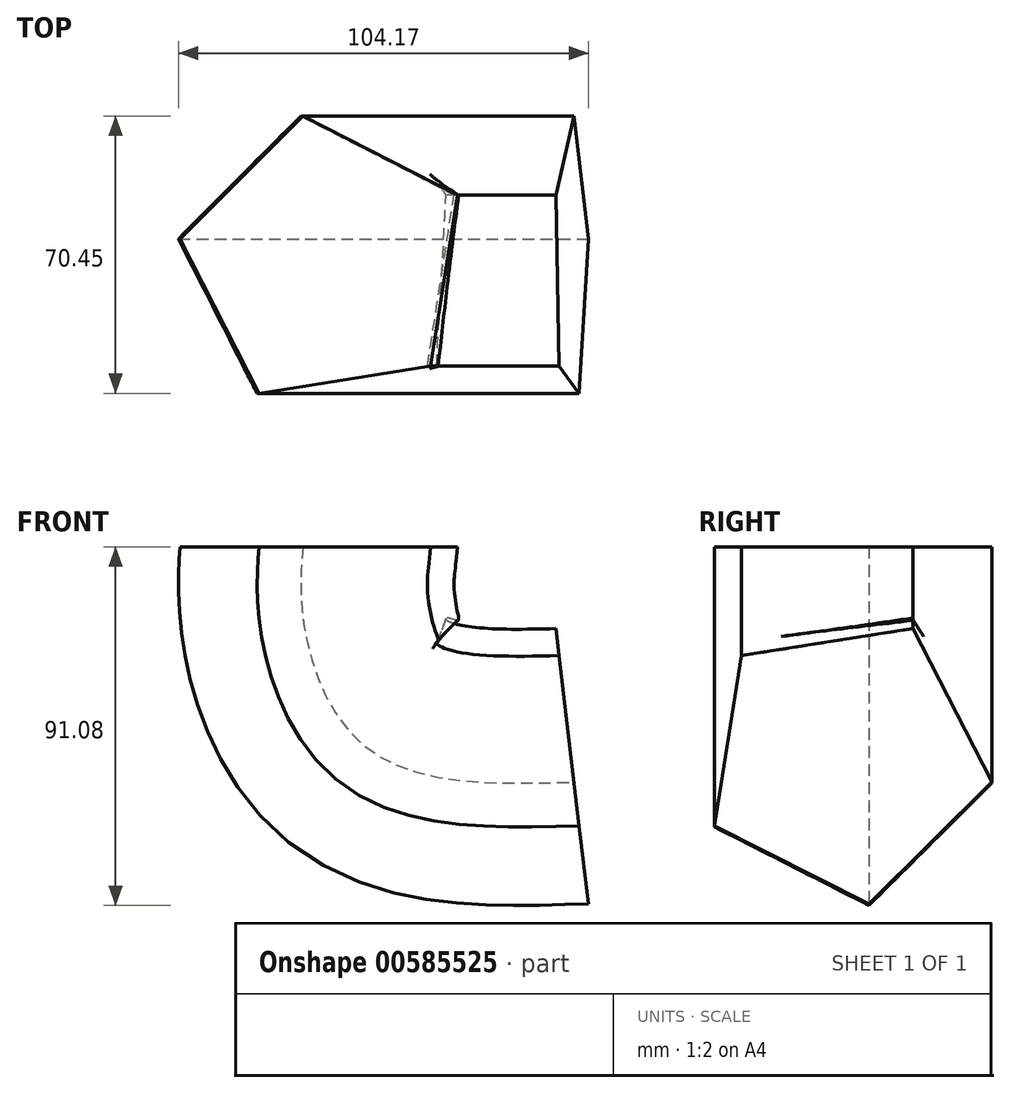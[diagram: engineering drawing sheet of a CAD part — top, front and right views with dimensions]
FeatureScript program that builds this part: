
annotation { "Feature Type Name" : "Feature", "Feature Type Description" : "" }
export const myFeature = defineFeature(function(context is Context, id is Id, definition is map)
    precondition{}
    {
        {
            var Q0;
            Q0=qCreatedBy(makeId("Top.planeOp"),FACE);
            var sketch = newSketch(context, id + "F0", { "sketchPlane" : qUnion([Q0])});
            skCircle(sketch, "E0.cCircle", {"center": v(0, 0) * mm, "radius": 30.34 * mm, "construction": true});
            skLineSegment(sketch, "E0.0", {"start": v(-37.04, 5.87) * mm, "end": v(-5.87, 37.04) * mm});
            skLineSegment(sketch, "E0.1", {"start": v(-5.87, 37.04) * mm, "end": v(33.41, 17.02) * mm});
            skLineSegment(sketch, "E0.2", {"start": v(33.41, 17.02) * mm, "end": v(26.51, -26.51) * mm});
            skLineSegment(sketch, "E0.3", {"start": v(26.51, -26.51) * mm, "end": v(-17.02, -33.41) * mm});
            skLineSegment(sketch, "E0.4", {"start": v(-17.02, -33.41) * mm, "end": v(-37.04, 5.87) * mm});
            skPoint(sketch, "E0.0.midPoint", {"position": v(-21.45, 21.45) * mm});
            skSolve(sketch);
        }
        {
            var Q0;
            Q0=qCreatedBy(makeId("Top.planeOp"),FACE);
            var sketch = newSketch(context, id + "F1", { "sketchPlane" : qUnion([Q0])});
            skCircle(sketch, "E1", {"center": v(0, 0) * mm, "radius": 22.6 * mm});
            skSolve(sketch);
        }
        {
            var Q0;
            Q0=qCreatedBy(makeId("Front.planeOp"),FACE);
            var sketch = newSketch(context, id + "F2", { "sketchPlane" : qUnion([Q0])});
            skFitSpline(sketch, "E2", {"points": [v(0, 0) * mm, v(0, -17.86) * mm, v(14.21, -46.64) * mm, v(62.31, -53.93) * mm], "startDerivative": vector(-5.87, -64.5) * mm, "endDerivative": vector(134.56, 3.66) * mm});
            skSolve(sketch);
        }
        {
            var Q0;
            Q0=makeQuery(id+"F0.imprint","IMPRINT",FACE,{"disambiguationData":[TD([[makeQuery(id+"F0.imprint","IMPRINT",EDGE,{"derivedFrom":sQuery(id+"F0.wireOp",EDGE,"E0.0")}),-1.0]])]});
            var Q1;
            Q1=sQuery(id+"F2.wireOp",EDGE,"E2");
            sweep(context, id + "F3", {"profiles" : qUnion([Q0]), "path" : qUnion([Q1])});
        }
    });
